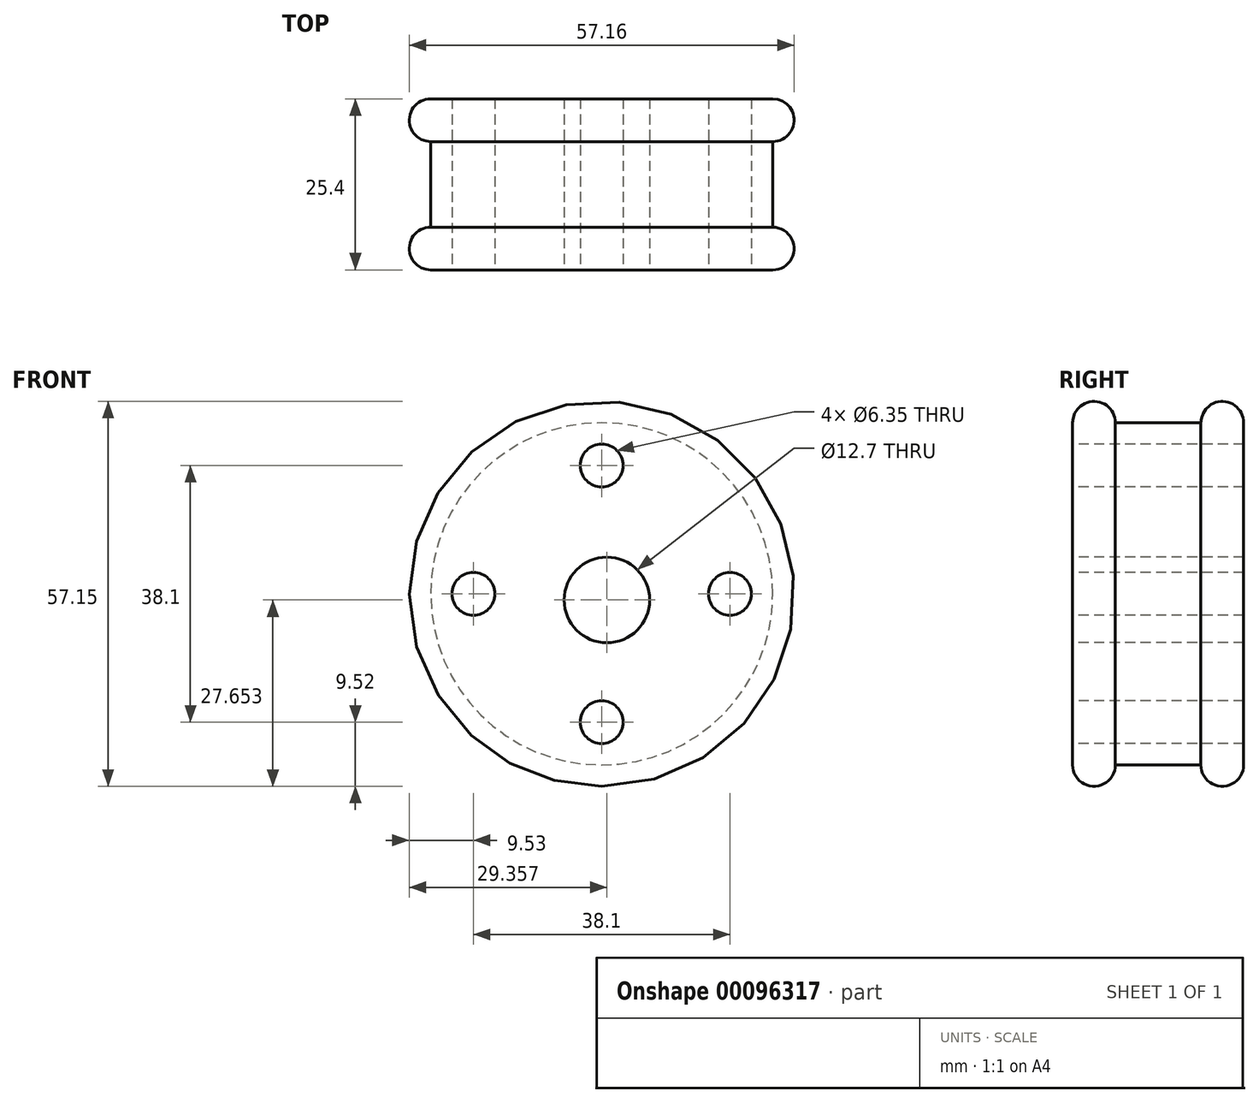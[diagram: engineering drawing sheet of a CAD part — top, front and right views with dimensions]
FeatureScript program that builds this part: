
annotation { "Feature Type Name" : "Feature", "Feature Type Description" : "" }
export const myFeature = defineFeature(function(context is Context, id is Id, definition is map)
    precondition{}
    {
        {
            var Q0;
            Q0=qCreatedBy(makeId("Front.planeOp"),FACE);
            var sketch = newSketch(context, id + "F0", { "sketchPlane" : qUnion([Q0])});
            skCircle(sketch, "E0", {"center": v(0, 0) * mm, "radius": 28.58 * mm});
            skSolve(sketch);
        }
        {
            var Q0;
            Q0 = qSketchRegion(id + "F0", true);
            extrude(context, id + "F1", {"entities" : qUnion([Q0]), "depth" : 6.35 * mm});
        }
        {
            var Q0;
            Q0=makeQuery(id+"F1.opExtrude","CAP_FACE",FACE,{"disambiguationData":[OSD([sQuery(id+"F0.wireOp",EDGE,"E0")])],"isStart":false});
            var sketch = newSketch(context, id + "F2", { "sketchPlane" : qUnion([Q0])});
            skCircle(sketch, "E1", {"center": v(0, 0) * mm, "radius": 25.4 * mm});
            skSolve(sketch);
        }
        {
            var Q0;
            Q0 = qSketchRegion(id + "F2", true);
            extrude(context, id + "F3", {"entities" : qUnion([Q0]), "operationType" : NewBodyOperationType.ADD, "depth" : 12.7 * mm});
        }
        {
            var Q0;
            Q0=makeQuery(id+"F3.opExtrude","CAP_FACE",FACE,{"disambiguationData":[OSD([sQuery(id+"F2.wireOp",EDGE,"E1")])],"isStart":false});
            var sketch = newSketch(context, id + "F4", { "sketchPlane" : qUnion([Q0])});
            skCircle(sketch, "E2.0", {"center": v(0, 0) * mm, "radius": 28.58 * mm});
            skSolve(sketch);
        }
        {
            var Q0;
            Q0 = qSketchRegion(id + "F4", true);
            extrude(context, id + "F5", {"entities" : qUnion([Q0]), "operationType" : NewBodyOperationType.ADD, "depth" : 6.35 * mm});
        }
        {
            var Q0;
            Q0=makeQuery(id+"F5.opExtrude","CAP_FACE",FACE,{"disambiguationData":[OSD([sQuery(id+"F4.wireOp",EDGE,"E2.0")])],"isStart":false});
            var sketch = newSketch(context, id + "F6", { "sketchPlane" : qUnion([Q0])});
            skCircle(sketch, "E3", {"center": v(0, 19.05) * mm, "radius": 3.18 * mm});
            skCircle(sketch, "E4", {"center": v(19.05, 0) * mm, "radius": 3.18 * mm});
            skCircle(sketch, "E5", {"center": v(0, -19.05) * mm, "radius": 3.18 * mm});
            skCircle(sketch, "E6", {"center": v(-19.05, 0) * mm, "radius": 3.18 * mm});
            skSolve(sketch);
        }
        {
            var Q0;
            Q0 = qSketchRegion(id + "F6", true);
            extrude(context, id + "F7", {"entities" : qUnion([Q0]), "operationType" : NewBodyOperationType.REMOVE, "endBound" : BoundingType.THROUGH_ALL, "oppositeDirection" : true, "depth" : 25.4 * mm});
        }
        {
            var Q0;
            Q0=makeQuery(id+"F5.opExtrude","CAP_EDGE",EDGE,{"disambiguationData":[OSD([sQuery(id+"F4.wireOp",EDGE,"E2.0")])],"isStart":false});
            var Q1;
            Q1=makeQuery(id+"F5.opExtrude","CAP_EDGE",EDGE,{"disambiguationData":[OSD([sQuery(id+"F4.wireOp",EDGE,"E2.0")])],"isStart":true});
            var Q2;
            Q2=makeQuery(id+"F1.opExtrude","CAP_EDGE",EDGE,{"disambiguationData":[OSD([sQuery(id+"F0.wireOp",EDGE,"E0")])],"isStart":false});
            var Q3;
            Q3=makeQuery(id+"F1.opExtrude","CAP_EDGE",EDGE,{"disambiguationData":[OSD([sQuery(id+"F0.wireOp",EDGE,"E0")])],"isStart":true});
            fillet(context, id + "F8", {"entities" : qUnion([Q0, Q1, Q2, Q3]), "radius" : 3.17 * mm, "tangentPropagation" : true, "allowEdgeOverflow" : false});
        }
        {
            var Q0;
            Q0=makeQuery(id+"F5.opExtrude","CAP_FACE",FACE,{"disambiguationData":[OSD([sQuery(id+"F4.wireOp",EDGE,"E2.0")])],"isStart":false});
            var sketch = newSketch(context, id + "F9", { "sketchPlane" : qUnion([Q0])});
            skCircle(sketch, "E7", {"center": v(0.78, -0.92) * mm, "radius": 6.35 * mm});
            skSolve(sketch);
        }
        {
            var Q0;
            Q0 = qSketchRegion(id + "F9", true);
            extrude(context, id + "F10", {"entities" : qUnion([Q0]), "operationType" : NewBodyOperationType.REMOVE, "endBound" : BoundingType.THROUGH_ALL, "oppositeDirection" : true, "depth" : 25.4 * mm});
        }
    });
